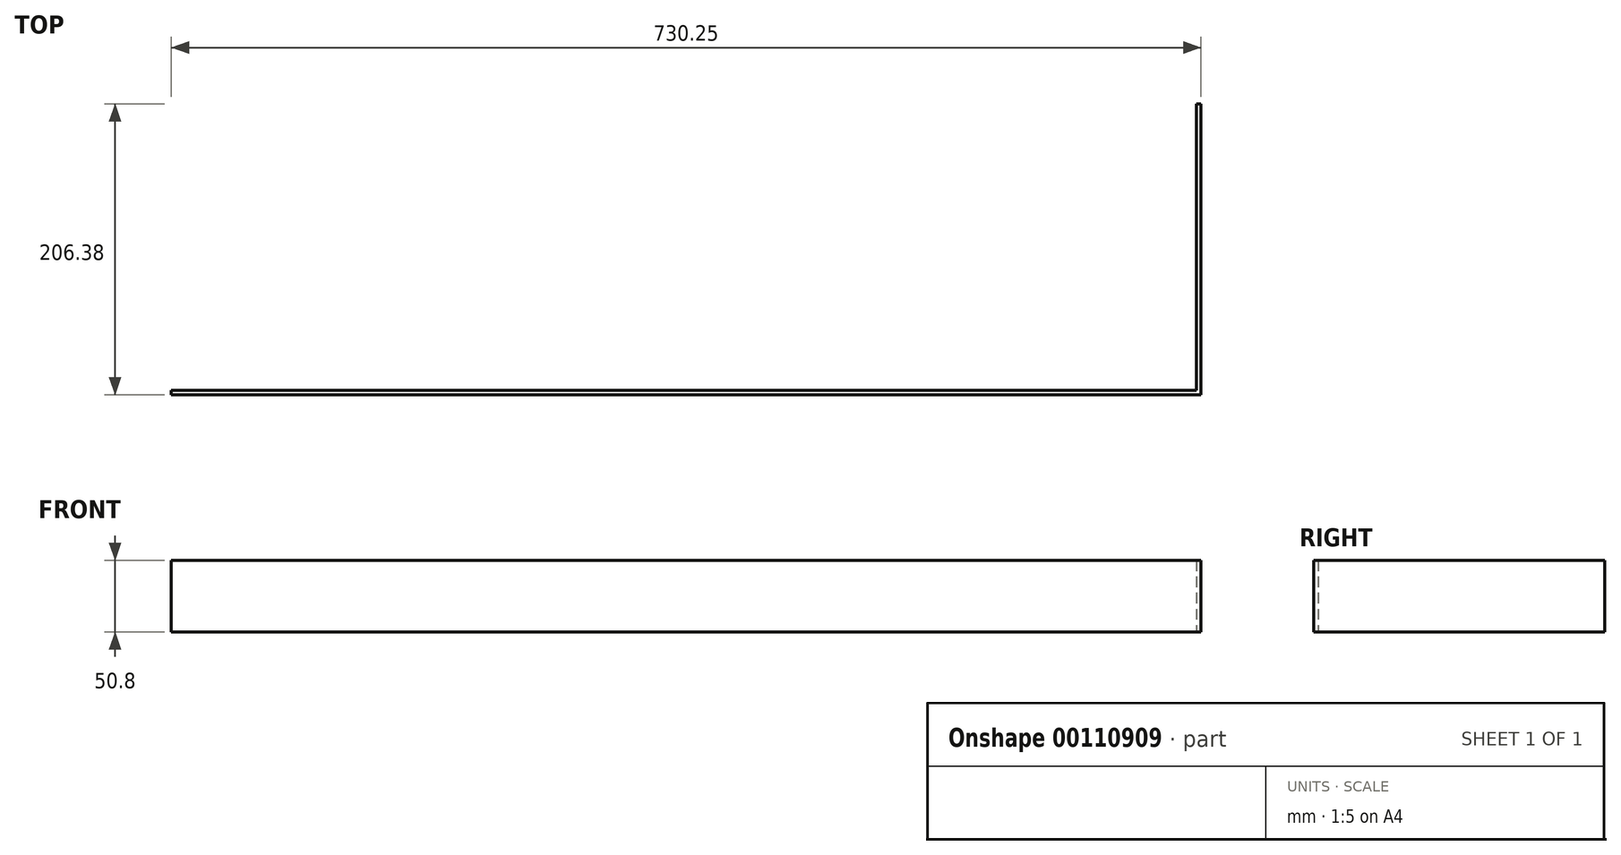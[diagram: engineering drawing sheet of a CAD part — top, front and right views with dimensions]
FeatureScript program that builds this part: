
annotation { "Feature Type Name" : "Feature", "Feature Type Description" : "" }
export const myFeature = defineFeature(function(context is Context, id is Id, definition is map)
    precondition{}
    {
        {
            var Q0;
            Q0=qCreatedBy(makeId("Top.planeOp"),FACE);
            var sketch = newSketch(context, id + "F0", { "sketchPlane" : qUnion([Q0])});
            skLineSegment(sketch, "E0.bottom", {"start": v(0, 0) * mm, "end": v(730.25, 0) * mm});
            skLineSegment(sketch, "E0.top", {"start": v(0, 3.18) * mm, "end": v(727.08, 3.18) * mm});
            skLineSegment(sketch, "E0.left", {"start": v(0, 0) * mm, "end": v(0, 3.18) * mm});
            skLineSegment(sketch, "E0.right", {"start": v(730.25, 0) * mm, "end": v(730.25, 3.18) * mm});
            skLineSegment(sketch, "E1.top", {"start": v(730.25, 206.38) * mm, "end": v(727.08, 206.38) * mm});
            skLineSegment(sketch, "E1.left", {"start": v(730.25, 3.17) * mm, "end": v(730.25, 206.38) * mm});
            skLineSegment(sketch, "E1.right", {"start": v(727.08, 3.18) * mm, "end": v(727.08, 206.38) * mm});
            skSolve(sketch);
        }
        {
            var Q0;
            Q0=qSketchRegion(id+"F0",true);
            extrude(context, id + "F1", {"entities" : qUnion([Q0]), "depth" : 50.8 * mm});
        }
    });
